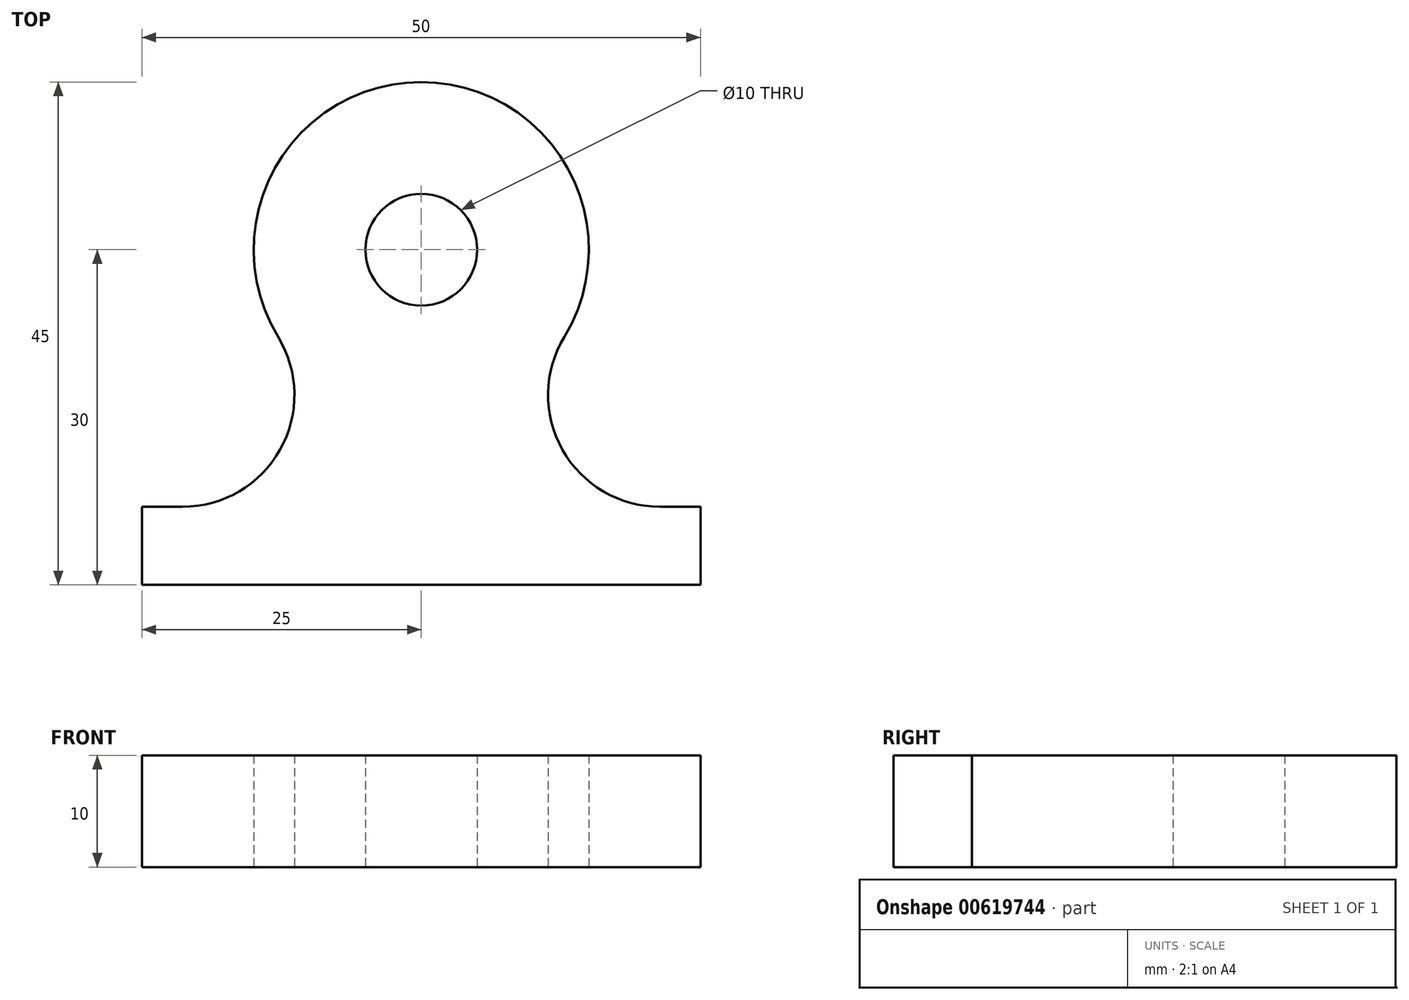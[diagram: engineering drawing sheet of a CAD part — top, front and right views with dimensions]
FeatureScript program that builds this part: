
annotation { "Feature Type Name" : "Feature", "Feature Type Description" : "" }
export const myFeature = defineFeature(function(context is Context, id is Id, definition is map)
    precondition{}
    {
        {
            var Q0;
            Q0=qCreatedBy(makeId("Top.planeOp"),FACE);
            var sketch = newSketch(context, id + "F0", { "sketchPlane" : qUnion([Q0])});
            skArc(sketch, "E0", {"start": v(12.81, 18.7) * mm, "mid": v(0, 41.5) * mm, "end": v(-12.81, 18.7) * mm});
            skLineSegment(sketch, "E1.bottom", {"start": v(-25, 3.5) * mm, "end": v(-21.35, 3.5) * mm});
            skLineSegment(sketch, "E1.top", {"start": v(-25, -3.5) * mm, "end": v(25, -3.5) * mm});
            skLineSegment(sketch, "E1.left", {"start": v(-25, 3.5) * mm, "end": v(-25, -3.5) * mm});
            skLineSegment(sketch, "E1.right", {"start": v(25, 3.5) * mm, "end": v(25, -3.5) * mm});
            skPoint(sketch, "E1.middle", {"position": v(0, 0) * mm});
            skArc(sketch, "E2", {"start": v(12.81, 18.7) * mm, "mid": v(12.64, 8.6) * mm, "end": v(21.35, 3.5) * mm});
            skArc(sketch, "E3", {"start": v(-21.35, 3.5) * mm, "mid": v(-12.64, 8.6) * mm, "end": v(-12.81, 18.7) * mm});
            skCircle(sketch, "E4", {"center": v(0, 26.5) * mm, "radius": 5 * mm});
            skLineSegment(sketch, "E5", {"start": v(0, 26.5) * mm, "end": v(0, 58.5) * mm, "construction": true});
            skLineSegment(sketch, "E6", {"start": v(0, 26.5) * mm, "end": v(0, -10.36) * mm});
            skPoint(sketch, "E6.endSnap0", {"position": v(0, -3.5) * mm});
            skLineSegment(sketch, "E7.trimOffspring", {"start": v(21.35, 3.5) * mm, "end": v(25, 3.5) * mm});
            skSolve(sketch);
        }
        {
            var Q0;
            Q0=makeQuery(id+"F0.imprint","IMPRINT",FACE,{"disambiguationData":[TD([[makeQuery(id+"F0.imprint","IMPRINT",EDGE,{"derivedFrom":sQuery(id+"F0.wireOp",EDGE,"E0")}),1.0]])]});
            extrude(context, id + "F1", {"entities" : qUnion([Q0]), "depth" : 10 * mm, "offsetDistance" : 25 * mm});
        }
    });
